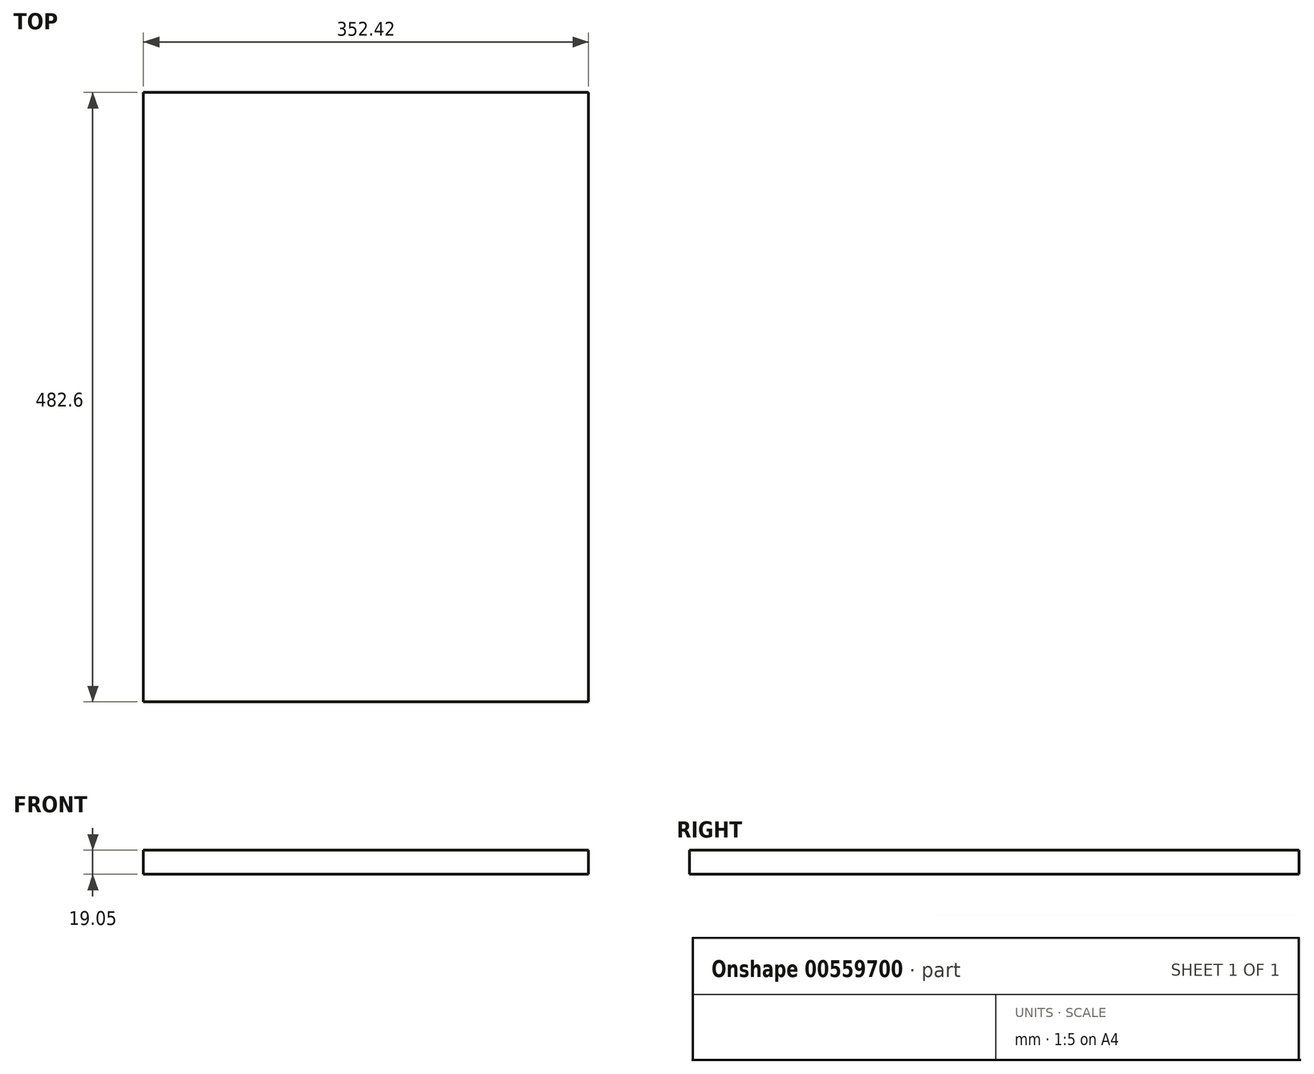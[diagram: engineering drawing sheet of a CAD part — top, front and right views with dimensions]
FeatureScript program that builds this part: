
annotation { "Feature Type Name" : "Feature", "Feature Type Description" : "" }
export const myFeature = defineFeature(function(context is Context, id is Id, definition is map)
    precondition{}
    {
        {
            var Q0;
            Q0=qCreatedBy(makeId("Top.planeOp"),FACE);
            var sketch = newSketch(context, id + "F0", { "sketchPlane" : qUnion([Q0])});
            skLineSegment(sketch, "E0.bottom", {"start": v(176.21, -241.3) * mm, "end": v(-176.21, -241.3) * mm});
            skLineSegment(sketch, "E0.top", {"start": v(176.21, 241.3) * mm, "end": v(-176.21, 241.3) * mm});
            skLineSegment(sketch, "E0.left", {"start": v(176.21, -241.3) * mm, "end": v(176.21, 241.3) * mm});
            skLineSegment(sketch, "E0.right", {"start": v(-176.21, -241.3) * mm, "end": v(-176.21, 241.3) * mm});
            skPoint(sketch, "E0.middle", {"position": v(0, 0) * mm});
            skSolve(sketch);
        }
        {
            var Q0;
            Q0 = qSketchRegion(id + "F0", true);
            extrude(context, id + "F1", {"entities" : qUnion([Q0]), "depth" : 19.05 * mm, "offsetDistance" : 25.4 * mm});
        }
    });
